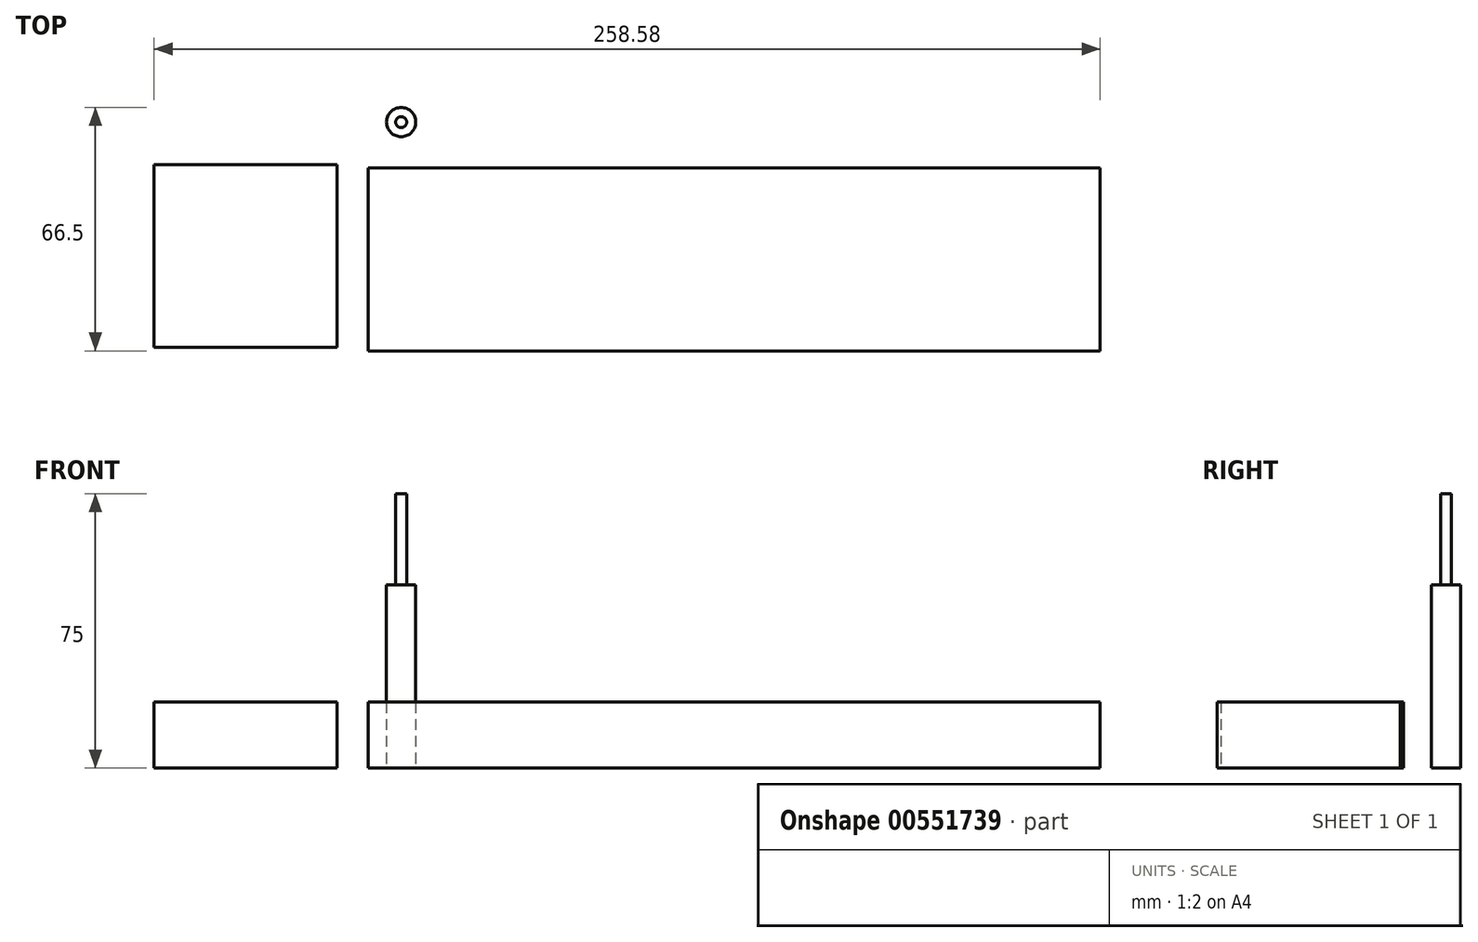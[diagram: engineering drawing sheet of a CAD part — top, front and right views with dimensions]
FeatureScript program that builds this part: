
annotation { "Feature Type Name" : "Feature", "Feature Type Description" : "" }
export const myFeature = defineFeature(function(context is Context, id is Id, definition is map)
    precondition{}
    {
        {
            var Q0;
            Q0=qCreatedBy(makeId("Top.planeOp"),FACE);
            var sketch = newSketch(context, id + "F0", { "sketchPlane" : qUnion([Q0])});
            skLineSegment(sketch, "E0.bottom", {"start": v(-29.78, 24.09) * mm, "end": v(170.22, 24.09) * mm});
            skLineSegment(sketch, "E0.top", {"start": v(-29.78, -25.91) * mm, "end": v(170.22, -25.91) * mm});
            skLineSegment(sketch, "E0.left", {"start": v(-29.78, 24.09) * mm, "end": v(-29.78, -25.91) * mm});
            skLineSegment(sketch, "E0.right", {"start": v(170.22, 24.09) * mm, "end": v(170.22, -25.91) * mm});
            skCircle(sketch, "E1", {"center": v(-20.82, 36.59) * mm, "radius": 4 * mm});
            skLineSegment(sketch, "E2.bottom", {"start": v(-88.36, 25.02) * mm, "end": v(-38.36, 25.02) * mm});
            skLineSegment(sketch, "E2.top", {"start": v(-88.36, -24.98) * mm, "end": v(-38.36, -24.98) * mm});
            skLineSegment(sketch, "E2.left", {"start": v(-88.36, 25.02) * mm, "end": v(-88.36, -24.98) * mm});
            skLineSegment(sketch, "E2.right", {"start": v(-38.36, 25.02) * mm, "end": v(-38.36, -24.98) * mm});
            skSolve(sketch);
        }
        {
            var Q0;
            Q0=makeQuery(id+"F0.imprint","IMPRINT",FACE,{"disambiguationData":[TD([[makeQuery(id+"F0.imprint","IMPRINT",EDGE,{"derivedFrom":sQuery(id+"F0.wireOp",EDGE,"E1")}),1.0]])]});
            extrude(context, id + "F1", {"entities" : qUnion([Q0]), "depth" : 50 * mm, "offsetDistance" : 25 * mm});
        }
        {
            var Q0;
            Q0=makeQuery(id+"F0.imprint","IMPRINT",FACE,{"disambiguationData":[TD([[makeQuery(id+"F0.imprint","IMPRINT",EDGE,{"derivedFrom":sQuery(id+"F0.wireOp",EDGE,"E0.bottom")}),-1.0]])]});
            var Q1;
            Q1=makeQuery(id+"F0.imprint","IMPRINT",FACE,{"disambiguationData":[TD([[makeQuery(id+"F0.imprint","IMPRINT",EDGE,{"derivedFrom":sQuery(id+"F0.wireOp",EDGE,"E2.bottom")}),-1.0]])]});
            extrude(context, id + "F2", {"entities" : qUnion([Q0, Q1]), "depth" : 18 * mm, "offsetDistance" : 25 * mm});
        }
        {
            var Q0;
            Q0=makeQuery(id+"F1.opExtrude","CAP_FACE",FACE,{"disambiguationData":[OSD([sQuery(id+"F0.wireOp",EDGE,"E1")])],"isStart":false});
            var sketch = newSketch(context, id + "F3", { "sketchPlane" : qUnion([Q0])});
            skCircle(sketch, "E3", {"center": v(-20.82, 36.59) * mm, "radius": 1.5 * mm});
            skSolve(sketch);
        }
        {
            var Q0;
            Q0 = qSketchRegion(id + "F3", true);
            extrude(context, id + "F4", {"entities" : qUnion([Q0]), "operationType" : NewBodyOperationType.ADD, "depth" : 25 * mm, "offsetDistance" : 25 * mm});
        }
    });
